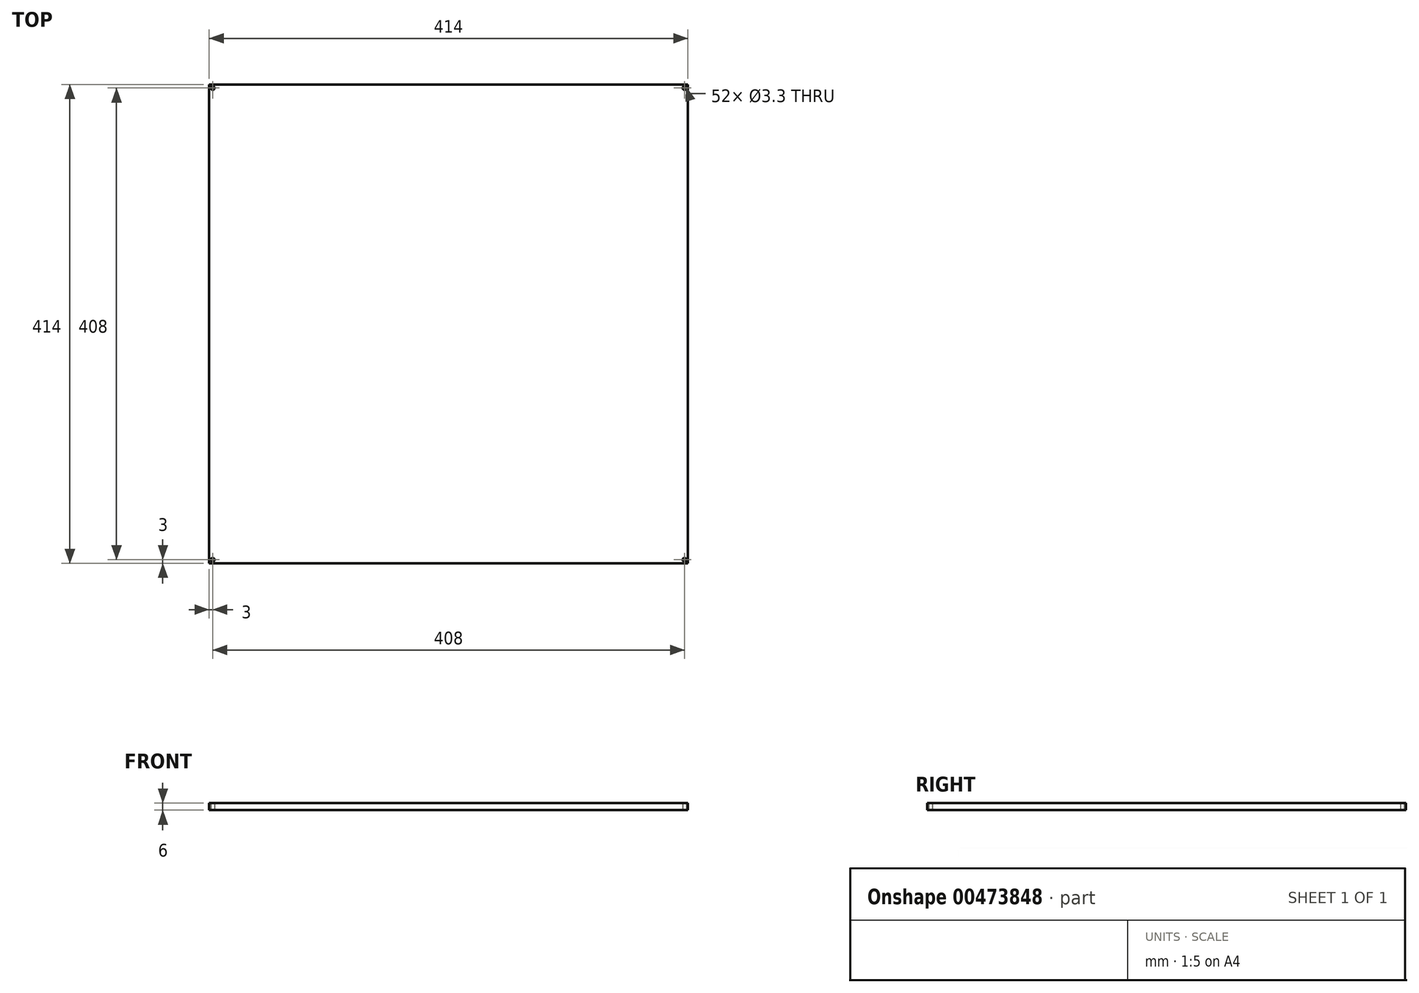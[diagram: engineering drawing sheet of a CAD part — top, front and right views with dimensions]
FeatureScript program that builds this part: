
annotation { "Feature Type Name" : "Feature", "Feature Type Description" : "" }
export const myFeature = defineFeature(function(context is Context, id is Id, definition is map)
    precondition{}
    {
        {
            var Q0;
            Q0=qCreatedBy(makeId("Top.planeOp"),FACE);
            var sketch = newSketch(context, id + "F0", { "sketchPlane" : qUnion([Q0])});
            skLineSegment(sketch, "E0.bottom", {"start": v(0, 0) * mm, "end": v(414, 0) * mm});
            skLineSegment(sketch, "E0.top", {"start": v(0, 414) * mm, "end": v(414, 414) * mm});
            skLineSegment(sketch, "E0.left", {"start": v(0, 0) * mm, "end": v(0, 414) * mm});
            skLineSegment(sketch, "E0.right", {"start": v(414, 0) * mm, "end": v(414, 414) * mm});
            skCircle(sketch, "E1", {"center": v(3, 411) * mm, "radius": 1.65 * mm});
            skCircle(sketch, "E2", {"center": v(411, 411) * mm, "radius": 1.65 * mm});
            skCircle(sketch, "E3", {"center": v(411, 3) * mm, "radius": 1.65 * mm});
            skCircle(sketch, "E4", {"center": v(3, 3) * mm, "radius": 1.65 * mm});
            skLineSegment(sketch, "E5", {"start": v(3, 411) * mm, "end": v(3, 414) * mm, "construction": true});
            skLineSegment(sketch, "E6", {"start": v(3, 411) * mm, "end": v(0, 411) * mm, "construction": true});
            skLineSegment(sketch, "E7", {"start": v(411, 411) * mm, "end": v(411, 414) * mm, "construction": true});
            skLineSegment(sketch, "E8", {"start": v(411, 411) * mm, "end": v(414, 411) * mm, "construction": true});
            skLineSegment(sketch, "E9", {"start": v(411, 3) * mm, "end": v(414, 3) * mm, "construction": true});
            skLineSegment(sketch, "E10", {"start": v(411, 3) * mm, "end": v(411, 0) * mm, "construction": true});
            skLineSegment(sketch, "E11", {"start": v(3, 3) * mm, "end": v(0, 3) * mm, "construction": true});
            skLineSegment(sketch, "E12", {"start": v(3, 3) * mm, "end": v(3, 0) * mm, "construction": true});
            skSolve(sketch);
        }
        {
            var Q0;
            Q0=qSketchRegion(id+"F0",true);
            extrude(context, id + "F1", {"entities" : qUnion([Q0]), "depth" : 6 * mm});
        }
    });
